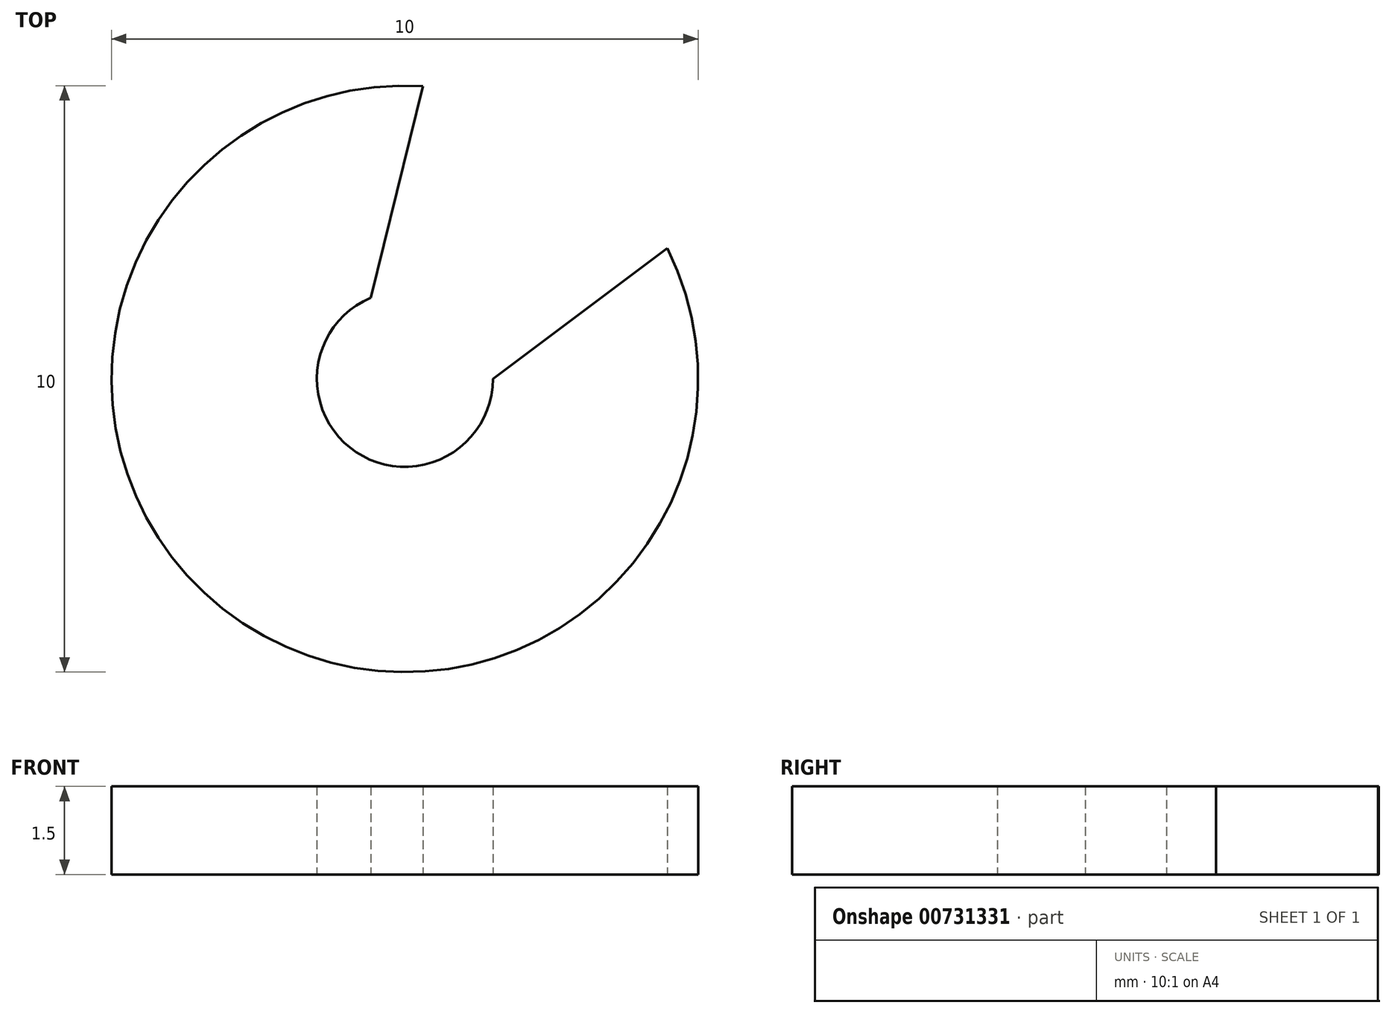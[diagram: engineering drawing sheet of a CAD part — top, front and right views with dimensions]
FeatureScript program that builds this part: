
annotation { "Feature Type Name" : "Feature", "Feature Type Description" : "" }
export const myFeature = defineFeature(function(context is Context, id is Id, definition is map)
    precondition{}
    {
        {
            assignVariable(context, id + "F0", {"name" : "mt", "anyValue" : 2 * mm});
        }
        {
            assignVariable(context, id + "F1", {"name" : "t", "anyValue" : 1.5 * mm});
        }
        {
            var Q0;
            Q0=qCreatedBy(makeId("Top.planeOp"),FACE);
            var sketch = newSketch(context, id + "F2", { "sketchPlane" : qUnion([Q0])});
            skCircle(sketch, "E0", {"center": v(0, 0) * mm, "radius": 5 * mm});
            skCircle(sketch, "E1", {"center": v(0, 0) * mm, "radius": 1.5 * mm});
            skLineSegment(sketch, "E2", {"start": v(0, 0) * mm, "end": v(2.76, 4.17) * mm});
            skLineSegment(sketch, "E3", {"start": v(0.31, 5) * mm, "end": v(4.48, 2.23) * mm});
            skLineSegment(sketch, "E4", {"start": v(-0.58, 1.38) * mm, "end": v(1.5, 0) * mm});
            skLineSegment(sketch, "E5", {"start": v(-0.58, 1.38) * mm, "end": v(0.31, 5) * mm});
            skLineSegment(sketch, "E6", {"start": v(1.5, 0) * mm, "end": v(4.48, 2.23) * mm});
            skSolve(sketch);
        }
        {
            var Q0;
            {var subQ0=sQuery(id+"F2.wireOp",EDGE,"E5");Q0=makeQuery(id+"F2.imprint","IMPRINT",FACE,{"disambiguationData":[TD([[makeQuery(id+"F2.imprint","IMPRINT",EDGE,{"derivedFrom":subQ0}),1.0]])]});}
            extrude(context, id + "F3", {"entities" : qUnion([Q0]), "depth" : getVariable(context, 't'), "offsetDistance" : 25 * mm});
        }
        {
            var Q0;
            Q0=makeQuery(id+"F3.opExtrude","CAP_FACE",FACE,{"disambiguationData":[OSD([sQuery(id+"F2.wireOp",EDGE,"E0"),sQuery(id+"F2.wireOp",EDGE,"E1"),sQuery(id+"F2.wireOp",EDGE,"E5"),sQuery(id+"F2.wireOp",EDGE,"E6")])],"isStart":false});
            var sketch = newSketch(context, id + "F4", { "sketchPlane" : qUnion([Q0])});
            skCircle(sketch, "E7", {"center": v(0, 0) * mm, "radius": 4 * mm});
            skSolve(sketch);
        }
        {
            var Q0;
            Q0 = qSketchRegion(id + "F4", true);
            extrude(context, id + "F5", {"entities" : qUnion([Q0]), "operationType" : NewBodyOperationType.REMOVE, "oppositeDirection" : true, "depth" : getVariable(context, 't') - getVariable(context, 'mt'), "offsetDistance" : 25 * mm});
        }
    });
